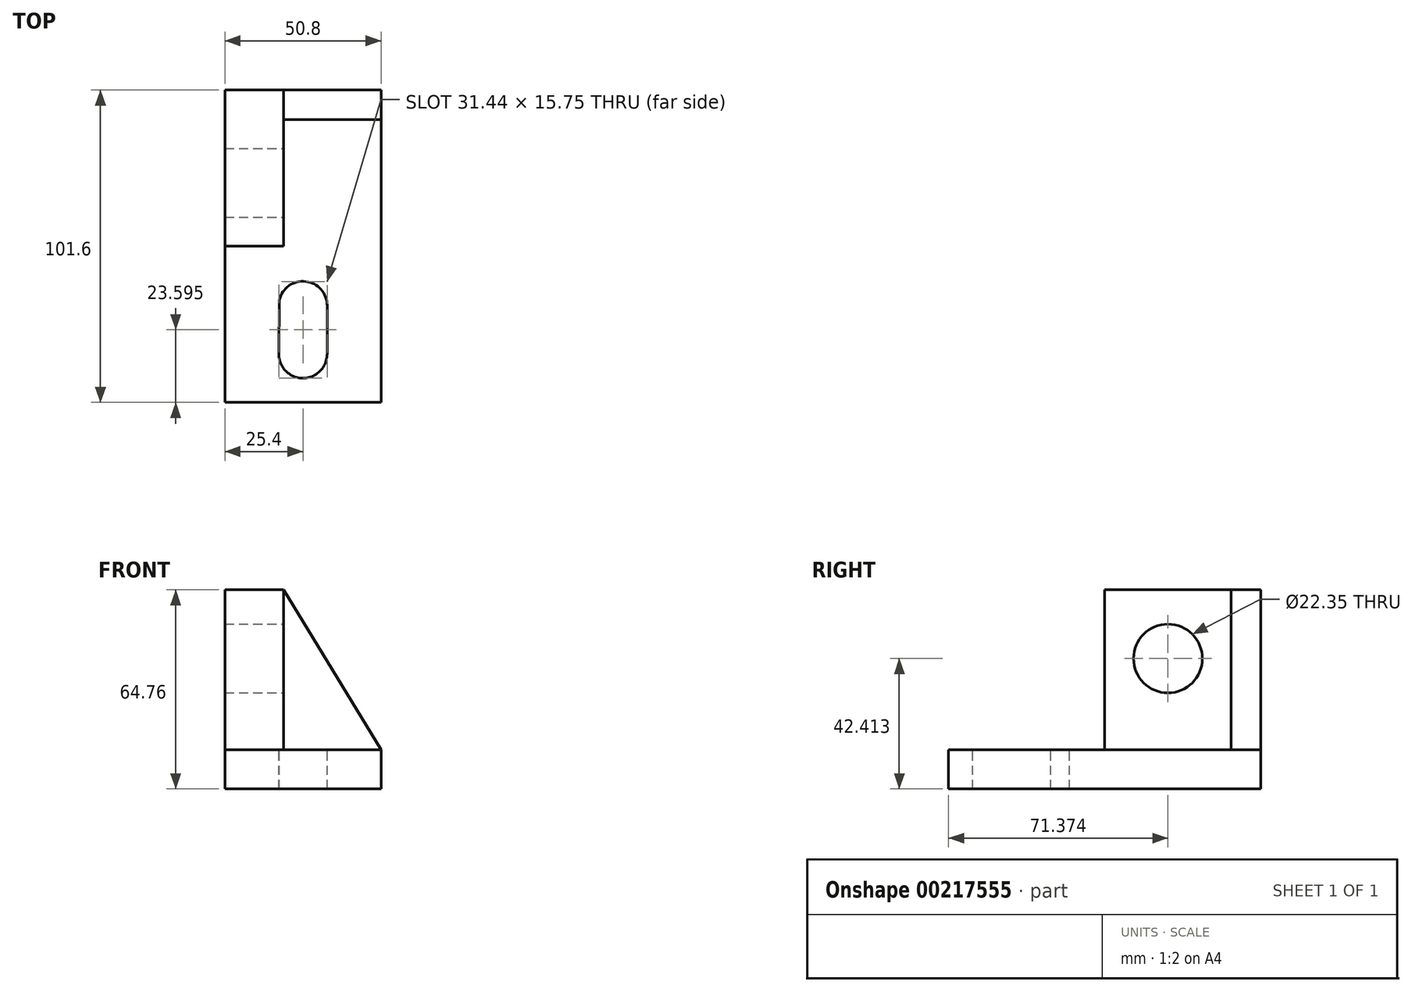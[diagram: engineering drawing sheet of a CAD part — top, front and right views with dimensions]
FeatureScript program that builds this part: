
annotation { "Feature Type Name" : "Feature", "Feature Type Description" : "" }
export const myFeature = defineFeature(function(context is Context, id is Id, definition is map)
    precondition{}
    {
        {
            var Q0;
            Q0=qCreatedBy(makeId("Right.planeOp"),FACE);
            var sketch = newSketch(context, id + "F0", { "sketchPlane" : qUnion([Q0])});
            skLineSegment(sketch, "E0.bottom", {"start": v(50.8, -32.39) * mm, "end": v(-50.8, -32.39) * mm});
            skLineSegment(sketch, "E0.top", {"start": v(50.8, 32.39) * mm, "end": v(-50.8, 32.38) * mm});
            skLineSegment(sketch, "E0.left", {"start": v(50.8, -32.39) * mm, "end": v(50.8, 32.39) * mm});
            skLineSegment(sketch, "E0.right", {"start": v(-50.8, -32.39) * mm, "end": v(-50.8, 32.38) * mm});
            skPoint(sketch, "E0.middle", {"position": v(0, 0) * mm});
            skSolve(sketch);
        }
        {
            var Q0;
            Q0=makeQuery(id+"F0.imprint","IMPRINT",FACE,{"disambiguationData":[TD([[makeQuery(id+"F0.imprint","IMPRINT",EDGE,{"derivedFrom":sQuery(id+"F0.wireOp",EDGE,"E0.bottom")}),-1.0]])]});
            extrude(context, id + "F1", {"entities" : qUnion([Q0]), "depth" : 50.8 * mm});
        }
        {
            var Q0;
            Q0=makeQuery(id+"F1.opExtrude","SWEPT_FACE",FACE,{"disambiguationData":[OSD([sQuery(id+"F0.wireOp",EDGE,"E0.top")])]});
            var sketch = newSketch(context, id + "F2", { "sketchPlane" : qUnion([Q0])});
            skLineSegment(sketch, "E1", {"start": v(0, 50.8) * mm, "end": v(0, 0) * mm});
            skLineSegment(sketch, "E2", {"start": v(0, 50.8) * mm, "end": v(19.05, 50.8) * mm});
            skLineSegment(sketch, "E3", {"start": v(19.05, 50.8) * mm, "end": v(19.05, 0) * mm});
            skLineSegment(sketch, "E4", {"start": v(19.05, 0) * mm, "end": v(0, 0) * mm});
            skSolve(sketch);
        }
        {
            var Q0;
            {var subQ4=sQuery(id+"F2.wireOp",EDGE,"E3");Q0=makeQuery(id+"F2.imprint","IMPRINT",FACE,{"disambiguationData":[TD([[makeQuery(id+"F2.imprint","IMPRINT",EDGE,{"derivedFrom":subQ4}),1.0]])]});}
            extrude(context, id + "F3", {"entities" : qUnion([Q0]), "operationType" : NewBodyOperationType.REMOVE, "oppositeDirection" : true, "depth" : 52.07 * mm});
        }
        {
            var Q0;
            Q0=makeQuery(id+"F3.boolean.opBoolean","COPY",FACE,{"derivedFrom":makeQuery(id+"F3.opExtrude","SWEPT_FACE",FACE,{"disambiguationData":[OSD([sQuery(id+"F2.wireOp",EDGE,"E3")])]})});
            var sketch = newSketch(context, id + "F4", { "sketchPlane" : qUnion([Q0])});
            skCircle(sketch, "E5", {"center": v(20.57, 10.03) * mm, "radius": 11.18 * mm});
            skSolve(sketch);
        }
        {
            var Q0;
            Q0=makeQuery(id+"F4.imprint","IMPRINT",FACE,{"disambiguationData":[TD([[makeQuery(id+"F4.imprint","IMPRINT",EDGE,{"derivedFrom":sQuery(id+"F4.wireOp",EDGE,"E5")}),1.0]])]});
            extrude(context, id + "F5", {"entities" : qUnion([Q0]), "operationType" : NewBodyOperationType.REMOVE, "endBound" : BoundingType.THROUGH_ALL, "oppositeDirection" : true, "depth" : 25.4 * mm});
        }
        {
            var Q0;
            Q0=makeQuery(id+"F3.boolean.opBoolean","COPY",FACE,{"derivedFrom":makeQuery(id+"F3.opExtrude","CAP_FACE",FACE,{"disambiguationData":[OSD([sQuery(id+"F0.wireOp",EDGE,"E0.top"),sQuery(id+"F0.wireOp",EDGE,"E0.left"),sQuery(id+"F0.wireOp",EDGE,"E0.right"),sQuery(id+"F2.wireOp",EDGE,"E3"),sQuery(id+"F2.wireOp",EDGE,"E4")])],"isStart":false})});
            var sketch = newSketch(context, id + "F6", { "sketchPlane" : qUnion([Q0])});
            skLineSegment(sketch, "E6", {"start": v(50.8, 50.8) * mm, "end": v(50.8, 41.15) * mm});
            skLineSegment(sketch, "E7", {"start": v(50.8, 41.15) * mm, "end": v(19.05, 41.15) * mm});
            skLineSegment(sketch, "E8", {"start": v(50.8, 50.8) * mm, "end": v(19.05, 50.8) * mm});
            skLineSegment(sketch, "E9", {"start": v(19.05, 50.8) * mm, "end": v(19.05, 41.15) * mm});
            skSolve(sketch);
        }
        {
            var Q0;
            Q0=makeQuery(id+"F6.imprint","IMPRINT",FACE,{"disambiguationData":[TD([[makeQuery(id+"F6.imprint","IMPRINT",EDGE,{"derivedFrom":sQuery(id+"F6.wireOp",EDGE,"E6")}),-1.0]])]});
            extrude(context, id + "F7", {"entities" : qUnion([Q0]), "operationType" : NewBodyOperationType.ADD, "depth" : 52.07 * mm});
        }
        {
            var Q0;
            Q0=makeQuery(id+"F7.opExtrude","SWEPT_FACE",FACE,{"disambiguationData":[OSD([sQuery(id+"F6.wireOp",EDGE,"E7")])]});
            var sketch = newSketch(context, id + "F8", { "sketchPlane" : qUnion([Q0])});
            skLineSegment(sketch, "E10", {"start": v(19.05, 32.38) * mm, "end": v(50.8, -19.68) * mm});
            skSolve(sketch);
        }
        {
            var Q0;
            Q0=makeQuery(id+"F8.imprint","IMPRINT",FACE,{"disambiguationData":[TD([[makeQuery(id+"F8.imprint","IMPRINT",EDGE,{"derivedFrom":sQuery(id+"F8.wireOp",EDGE,"E10")}),1.0]])]});
            extrude(context, id + "F9", {"entities" : qUnion([Q0]), "operationType" : NewBodyOperationType.REMOVE, "endBound" : BoundingType.THROUGH_ALL, "oppositeDirection" : true, "depth" : 25.4 * mm});
        }
        {
            var Q0;
            Q0=makeQuery(id+"F3.boolean.opBoolean","COPY",FACE,{"derivedFrom":makeQuery(id+"F3.opExtrude","CAP_FACE",FACE,{"disambiguationData":[OSD([sQuery(id+"F0.wireOp",EDGE,"E0.top"),sQuery(id+"F0.wireOp",EDGE,"E0.left"),sQuery(id+"F0.wireOp",EDGE,"E0.right"),sQuery(id+"F2.wireOp",EDGE,"E3"),sQuery(id+"F2.wireOp",EDGE,"E4")])],"isStart":false})});
            var sketch = newSketch(context, id + "F10", { "sketchPlane" : qUnion([Q0])});
            skLineSegment(sketch, "E11", {"start": v(25.4, -50.8) * mm, "end": v(25.4, -35.05) * mm});
            skArc(sketch, "E12", {"start": v(17.53, -34.96) * mm, "mid": v(25.35, -42.93) * mm, "end": v(33.27, -35.05) * mm});
            skArc(sketch, "E13", {"start": v(33.27, -19.35) * mm, "mid": v(26.31, -11.48) * mm, "end": v(17.73, -17.53) * mm});
            skLineSegment(sketch, "E14", {"start": v(17.73, -17.53) * mm, "end": v(17.53, -34.96) * mm});
            skLineSegment(sketch, "E15", {"start": v(33.27, -19.35) * mm, "end": v(33.27, -35.05) * mm});
            skSolve(sketch);
        }
        {
            var Q0;
            Q0=makeQuery(id+"F10.imprint","IMPRINT",FACE,{"disambiguationData":[TD([[makeQuery(id+"F10.imprint","IMPRINT",EDGE,{"derivedFrom":sQuery(id+"F10.wireOp",EDGE,"E13")}),1.0]])]});
            extrude(context, id + "F11", {"entities" : qUnion([Q0]), "operationType" : NewBodyOperationType.REMOVE, "endBound" : BoundingType.THROUGH_ALL, "oppositeDirection" : true, "depth" : 25.4 * mm});
        }
    });
